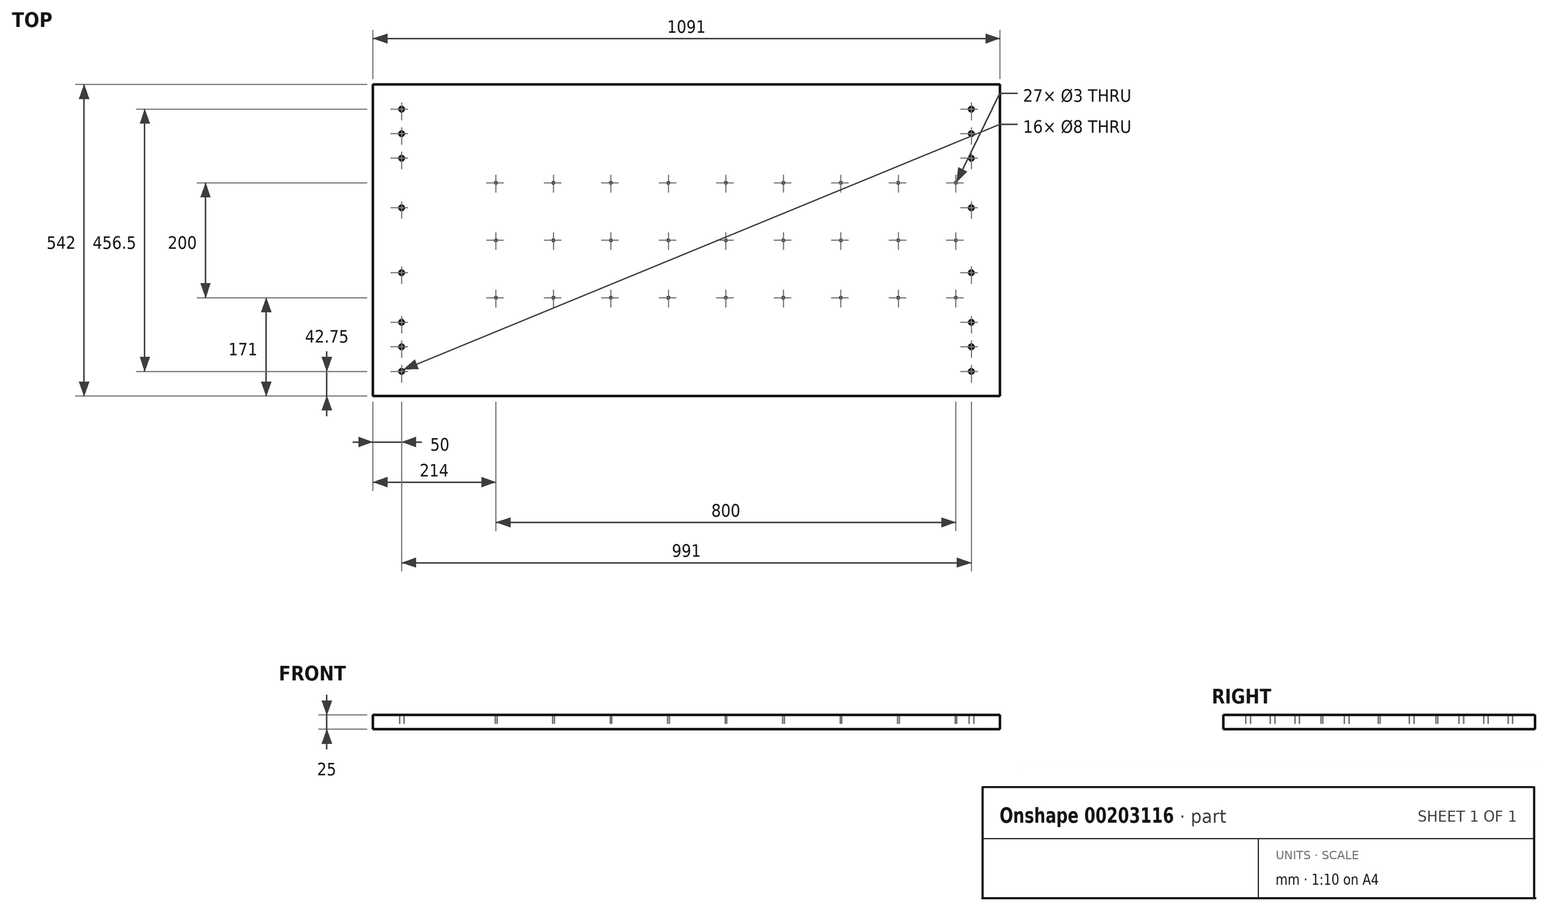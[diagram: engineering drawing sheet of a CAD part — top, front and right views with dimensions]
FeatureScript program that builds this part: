
annotation { "Feature Type Name" : "Feature", "Feature Type Description" : "" }
export const myFeature = defineFeature(function(context is Context, id is Id, definition is map)
    precondition{}
    {
        {
            var Q0;
            Q0=qCreatedBy(makeId("Top.planeOp"),FACE);
            var sketch = newSketch(context, id + "F0", { "sketchPlane" : qUnion([Q0])});
            skLineSegment(sketch, "E0.bottom", {"start": v(0, 0) * mm, "end": v(1091, 0) * mm});
            skLineSegment(sketch, "E0.top", {"start": v(0, 542) * mm, "end": v(1091, 542) * mm});
            skLineSegment(sketch, "E0.left", {"start": v(0, 0) * mm, "end": v(0, 542) * mm});
            skLineSegment(sketch, "E0.right", {"start": v(1091, 0) * mm, "end": v(1091, 542) * mm});
            skPoint(sketch, "E1", {"position": v(214, 171) * mm});
            skPoint(sketch, "E2", {"position": v(214, 271) * mm});
            skPoint(sketch, "E3", {"position": v(214, 371) * mm});
            skLineSegment(sketch, "E4", {"start": v(-315.3, 371) * mm, "end": v(-315.3, 271) * mm, "construction": true});
            skLineSegment(sketch, "E5", {"start": v(-315.3, 271) * mm, "end": v(-315.3, 171) * mm, "construction": true});
            skLineSegment(sketch, "E6", {"start": v(-315.3, 171) * mm, "end": v(-315.3, 0) * mm, "construction": true});
            skLineSegment(sketch, "E7", {"start": v(-315.3, 542) * mm, "end": v(-315.3, 371) * mm, "construction": true});
            skPoint(sketch, "E8", {"position": v(-315.3, 456.5) * mm});
            skPoint(sketch, "E9", {"position": v(-315.3, 327.44) * mm});
            skPoint(sketch, "E10", {"position": v(-315.3, 221) * mm});
            skPoint(sketch, "E11", {"position": v(-315.3, 85.5) * mm});
            skLineSegment(sketch, "E12", {"start": v(50, 327.44) * mm, "end": v(1041, 327.44) * mm, "construction": true});
            skLineSegment(sketch, "E13", {"start": v(50, 456.5) * mm, "end": v(1041, 456.5) * mm, "construction": true});
            skLineSegment(sketch, "E14", {"start": v(1046.67, 271) * mm, "end": v(1429.51, 271) * mm, "construction": true});
            skPoint(sketch, "E14.endSnap0", {"position": v(1091, 271) * mm});
            skLineSegment(sketch, "E15", {"start": v(-218.04, 542) * mm, "end": v(-218.04, 456.5) * mm, "construction": true});
            skPoint(sketch, "E16", {"position": v(-218.04, 499.25) * mm});
            skLineSegment(sketch, "E17", {"start": v(50, 499.25) * mm, "end": v(1041, 499.25) * mm, "construction": true});
            skLineSegment(sketch, "E18", {"start": v(-218.04, 456.5) * mm, "end": v(-218.04, 371) * mm, "construction": true});
            skPoint(sketch, "E19", {"position": v(-218.04, 413.75) * mm});
            skLineSegment(sketch, "E20", {"start": v(50, 413.75) * mm, "end": v(1041, 413.75) * mm, "construction": true});
            skLineSegment(sketch, "E21.MirrorCS", {"start": v(50, 42.75) * mm, "end": v(1041, 42.75) * mm, "construction": true});
            skLineSegment(sketch, "E22.MirrorCS", {"start": v(50, 85.5) * mm, "end": v(1041, 85.5) * mm, "construction": true});
            skLineSegment(sketch, "E23.MirrorCS", {"start": v(50, 128.25) * mm, "end": v(1041, 128.25) * mm, "construction": true});
            skLineSegment(sketch, "E24.MirrorCS", {"start": v(50, 214.56) * mm, "end": v(1041, 214.56) * mm, "construction": true});
            skSolve(sketch);
        }
        {
            var Q0;
            Q0=makeQuery(id+"F0.imprint","IMPRINT",FACE,{"disambiguationData":[TD([[makeQuery(id+"F0.imprint","IMPRINT",EDGE,{"derivedFrom":sQuery(id+"F0.wireOp",EDGE,"E0.bottom")}),1.0]])]});
            var sketch = newSketch(context, id + "F1", { "sketchPlane" : qUnion([Q0])});
            skLineSegment(sketch, "E25.bottom", {"start": v(0, 0) * mm, "end": v(1091, 0) * mm});
            skLineSegment(sketch, "E25.top", {"start": v(0, 542) * mm, "end": v(1091, 542) * mm});
            skLineSegment(sketch, "E25.left", {"start": v(0, 0) * mm, "end": v(0, 542) * mm});
            skLineSegment(sketch, "E25.right", {"start": v(1091, 0) * mm, "end": v(1091, 542) * mm});
            skCircle(sketch, "E26", {"center": v(214, 171) * mm, "radius": 1.5 * mm});
            skCircle(sketch, "E27.0.1.1", {"center": v(214, 271) * mm, "radius": 1.5 * mm});
            skCircle(sketch, "E27.0.2.1", {"center": v(214, 371) * mm, "radius": 1.5 * mm});
            skCircle(sketch, "E27.1.0.1", {"center": v(314, 171) * mm, "radius": 1.5 * mm});
            skCircle(sketch, "E27.1.1.1", {"center": v(314, 271) * mm, "radius": 1.5 * mm});
            skCircle(sketch, "E27.1.2.1", {"center": v(314, 371) * mm, "radius": 1.5 * mm});
            skCircle(sketch, "E27.2.0.1", {"center": v(414, 171) * mm, "radius": 1.5 * mm});
            skCircle(sketch, "E27.2.1.1", {"center": v(414, 271) * mm, "radius": 1.5 * mm});
            skCircle(sketch, "E27.2.2.1", {"center": v(414, 371) * mm, "radius": 1.5 * mm});
            skCircle(sketch, "E27.3.0.1", {"center": v(514, 171) * mm, "radius": 1.5 * mm});
            skCircle(sketch, "E27.3.1.1", {"center": v(514, 271) * mm, "radius": 1.5 * mm});
            skCircle(sketch, "E27.3.2.1", {"center": v(514, 371) * mm, "radius": 1.5 * mm});
            skCircle(sketch, "E27.4.0.1", {"center": v(614, 171) * mm, "radius": 1.5 * mm});
            skCircle(sketch, "E27.4.1.1", {"center": v(614, 271) * mm, "radius": 1.5 * mm});
            skCircle(sketch, "E27.4.2.1", {"center": v(614, 371) * mm, "radius": 1.5 * mm});
            skCircle(sketch, "E27.5.0.1", {"center": v(714, 171) * mm, "radius": 1.5 * mm});
            skCircle(sketch, "E27.5.1.1", {"center": v(714, 271) * mm, "radius": 1.5 * mm});
            skCircle(sketch, "E27.5.2.1", {"center": v(714, 371) * mm, "radius": 1.5 * mm});
            skCircle(sketch, "E27.6.0.1", {"center": v(814, 171) * mm, "radius": 1.5 * mm});
            skCircle(sketch, "E27.6.1.1", {"center": v(814, 271) * mm, "radius": 1.5 * mm});
            skCircle(sketch, "E27.6.2.1", {"center": v(814, 371) * mm, "radius": 1.5 * mm});
            skCircle(sketch, "E27.7.0.1", {"center": v(914, 171) * mm, "radius": 1.5 * mm});
            skCircle(sketch, "E27.7.1.1", {"center": v(914, 271) * mm, "radius": 1.5 * mm});
            skCircle(sketch, "E27.7.2.1", {"center": v(914, 371) * mm, "radius": 1.5 * mm});
            skCircle(sketch, "E27.8.0.1", {"center": v(1014, 171) * mm, "radius": 1.5 * mm});
            skCircle(sketch, "E27.8.1.1", {"center": v(1014, 271) * mm, "radius": 1.5 * mm});
            skCircle(sketch, "E27.8.2.1", {"center": v(1014, 371) * mm, "radius": 1.5 * mm});
            skLineSegment(sketch, "E27.direction1", {"start": v(214, 171) * mm, "end": v(314, 171) * mm, "construction": true});
            skLineSegment(sketch, "E27.direction2", {"start": v(214, 171) * mm, "end": v(214, 271) * mm, "construction": true});
            skCircle(sketch, "E28", {"center": v(50, 499.25) * mm, "radius": 4 * mm});
            skCircle(sketch, "E29", {"center": v(50, 456.5) * mm, "radius": 4 * mm});
            skCircle(sketch, "E30", {"center": v(50, 413.75) * mm, "radius": 4 * mm});
            skCircle(sketch, "E31", {"center": v(50, 327.44) * mm, "radius": 4 * mm});
            skCircle(sketch, "E32", {"center": v(50, 214.56) * mm, "radius": 4 * mm});
            skCircle(sketch, "E33", {"center": v(50, 128.25) * mm, "radius": 4 * mm});
            skCircle(sketch, "E34", {"center": v(50, 85.5) * mm, "radius": 4 * mm});
            skCircle(sketch, "E35", {"center": v(50, 42.75) * mm, "radius": 4 * mm});
            skLineSegment(sketch, "E36", {"start": v(545.5, -52.3) * mm, "end": v(545.5, -207.42) * mm, "construction": true});
            skPoint(sketch, "E36.startSnap0", {"position": v(545.5, 0) * mm});
            skCircle(sketch, "E37.MirrorC", {"center": v(1041, 42.75) * mm, "radius": 4 * mm});
            skCircle(sketch, "E38.MirrorC", {"center": v(1041, 85.5) * mm, "radius": 4 * mm});
            skCircle(sketch, "E39.MirrorC", {"center": v(1041, 499.25) * mm, "radius": 4 * mm});
            skCircle(sketch, "E40.MirrorC", {"center": v(1041, 413.75) * mm, "radius": 4 * mm});
            skCircle(sketch, "E41.MirrorC", {"center": v(1041, 214.56) * mm, "radius": 4 * mm});
            skCircle(sketch, "E42.MirrorC", {"center": v(1041, 327.44) * mm, "radius": 4 * mm});
            skCircle(sketch, "E43.MirrorC", {"center": v(1041, 456.5) * mm, "radius": 4 * mm});
            skCircle(sketch, "E44.MirrorC", {"center": v(1041, 128.25) * mm, "radius": 4 * mm});
            skSolve(sketch);
        }
        {
            var Q0;
            Q0=makeQuery(id+"F1.imprint","IMPRINT",FACE,{"disambiguationData":[TD([[makeQuery(id+"F1.imprint","IMPRINT",EDGE,{"derivedFrom":sQuery(id+"F1.wireOp",EDGE,"E25.bottom")}),1.0]])]});
            extrude(context, id + "F2", {"entities" : qUnion([Q0]), "depth" : 25 * mm});
        }
    });
